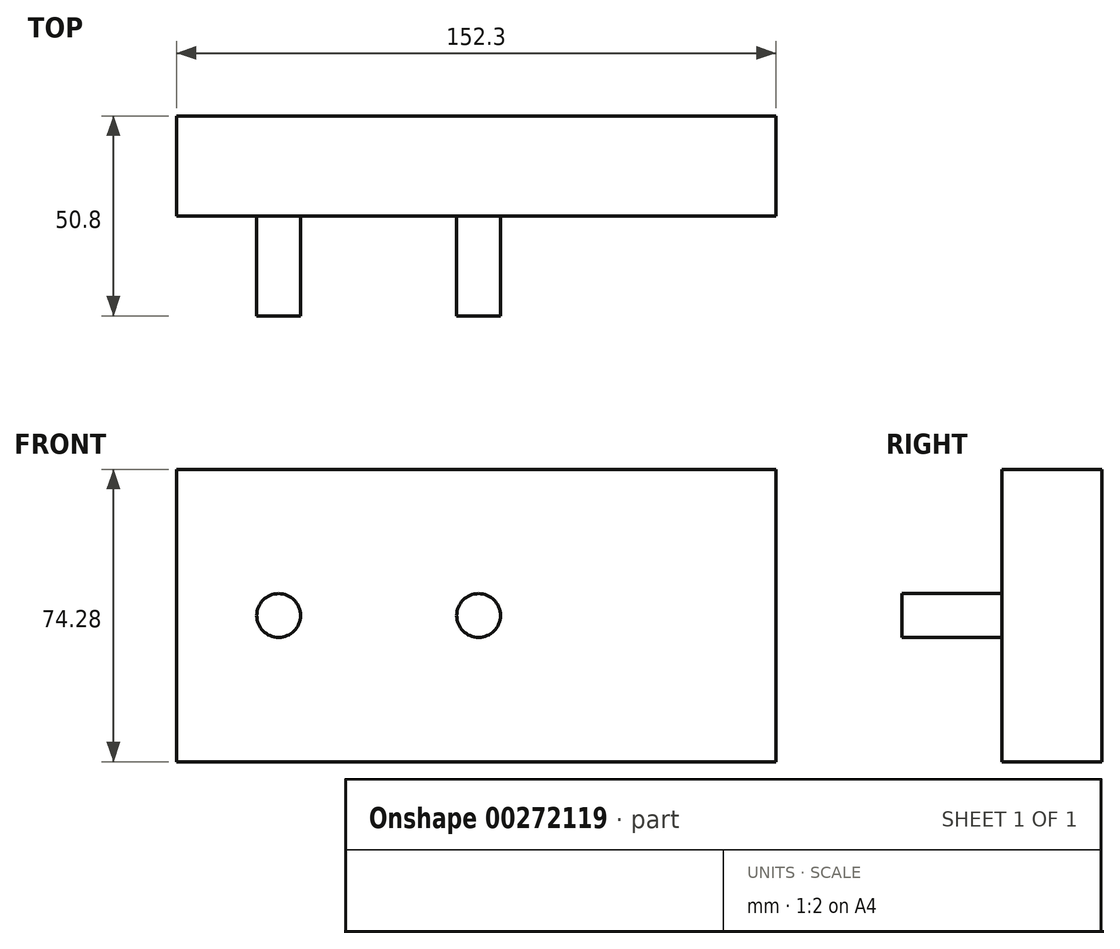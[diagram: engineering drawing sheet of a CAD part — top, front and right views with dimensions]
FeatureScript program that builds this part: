
annotation { "Feature Type Name" : "Feature", "Feature Type Description" : "" }
export const myFeature = defineFeature(function(context is Context, id is Id, definition is map)
    precondition{}
    {
        {
            var Q0;
            Q0=qCreatedBy(makeId("Front.planeOp"),FACE);
            var sketch = newSketch(context, id + "F0", { "sketchPlane" : qUnion([Q0])});
            skLineSegment(sketch, "E0.bottom", {"start": v(0, 0) * mm, "end": v(152.3, 0) * mm});
            skLineSegment(sketch, "E0.top", {"start": v(0, 74.28) * mm, "end": v(152.3, 74.28) * mm});
            skLineSegment(sketch, "E0.left", {"start": v(0, 0) * mm, "end": v(0, 74.28) * mm});
            skLineSegment(sketch, "E0.right", {"start": v(152.3, 0) * mm, "end": v(152.3, 74.28) * mm});
            skSolve(sketch);
        }
        {
            var Q0;
            Q0=makeQuery(id+"F0.imprint","IMPRINT",FACE,{"disambiguationData":[TD([[makeQuery(id+"F0.imprint","IMPRINT",EDGE,{"derivedFrom":sQuery(id+"F0.wireOp",EDGE,"E0.bottom")}),1.0]])]});
            extrude(context, id + "F1", {"entities" : qUnion([Q0]), "depth" : 25.4 * mm});
        }
        {
            var Q0;
            Q0=makeQuery(id+"F1.opExtrude","CAP_FACE",FACE,{"disambiguationData":[OSD([sQuery(id+"F0.wireOp",EDGE,"E0.bottom"),sQuery(id+"F0.wireOp",EDGE,"E0.top"),sQuery(id+"F0.wireOp",EDGE,"E0.left"),sQuery(id+"F0.wireOp",EDGE,"E0.right")])],"isStart":false});
            var sketch = newSketch(context, id + "F2", { "sketchPlane" : qUnion([Q0])});
            skCircle(sketch, "E1", {"center": v(25.97, 37.14) * mm, "radius": 5.56 * mm});
            skPoint(sketch, "E1.centerSnap0", {"position": v(0, 37.14) * mm});
            skLineSegment(sketch, "E2", {"start": v(25.97, 37.14) * mm, "end": v(76.77, 37.14) * mm, "construction": true});
            skCircle(sketch, "E3", {"center": v(76.77, 37.14) * mm, "radius": 5.56 * mm});
            skSolve(sketch);
        }
        {
            var Q0;
            Q0=makeQuery(id+"F2.imprint","IMPRINT",FACE,{"disambiguationData":[TD([[makeQuery(id+"F2.imprint","IMPRINT",EDGE,{"derivedFrom":sQuery(id+"F2.wireOp",EDGE,"E1")}),1.0]])]});
            var Q1;
            Q1=makeQuery(id+"F2.imprint","IMPRINT",FACE,{"disambiguationData":[TD([[makeQuery(id+"F2.imprint","IMPRINT",EDGE,{"derivedFrom":sQuery(id+"F2.wireOp",EDGE,"E3")}),1.0]])]});
            var Q2;
            Q2=sQuery(id+"F2.wireOp",EDGE,"E1");
            var Q3;
            Q3=sQuery(id+"F2.wireOp",EDGE,"E3");
            extrude(context, id + "F3", {"entities" : qUnion([Q0, Q1]), "surfaceEntities" : qUnion([Q2, Q3]), "depth" : 25.4 * mm});
        }
    });
